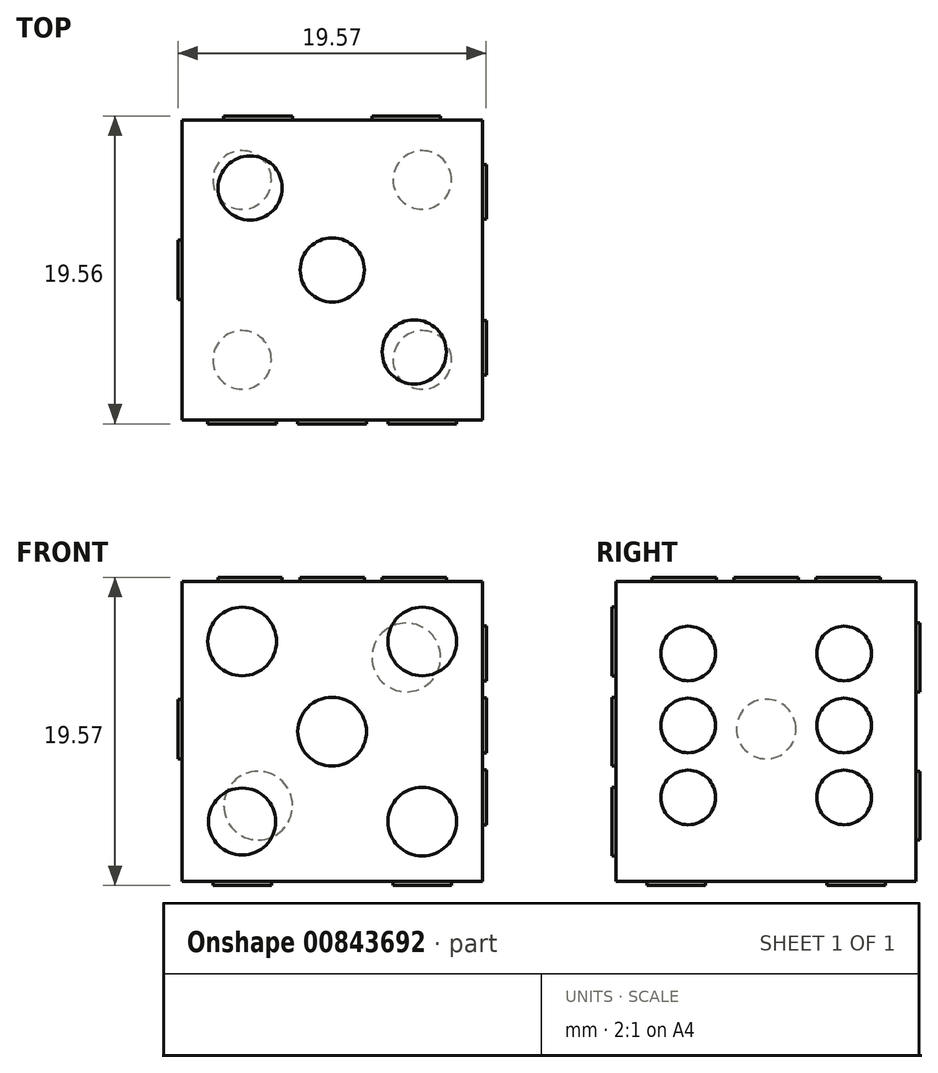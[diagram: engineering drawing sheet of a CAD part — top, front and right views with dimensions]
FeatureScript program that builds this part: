
annotation { "Feature Type Name" : "Feature", "Feature Type Description" : "" }
export const myFeature = defineFeature(function(context is Context, id is Id, definition is map)
    precondition{}
    {
        {
            var Q0;
            Q0=qCreatedBy(makeId("Front.planeOp"),FACE);
            var sketch = newSketch(context, id + "F0", { "sketchPlane" : qUnion([Q0])});
            skLineSegment(sketch, "E0", {"start": v(1.99, 4.8) * mm, "end": v(1.99, 23.85) * mm});
            skLineSegment(sketch, "E1", {"start": v(1.99, 23.85) * mm, "end": v(21.05, 23.85) * mm});
            skLineSegment(sketch, "E2", {"start": v(21.05, 23.85) * mm, "end": v(21.05, 4.8) * mm});
            skLineSegment(sketch, "E3", {"start": v(21.05, 4.8) * mm, "end": v(1.99, 4.8) * mm});
            skSolve(sketch);
        }
        {
            var Q0;
            Q0 = qSketchRegion(id + "F0", true);
            extrude(context, id + "F1", {"entities" : qUnion([Q0]), "endBound" : BoundingType.SYMMETRIC, "depth" : 19.05 * mm, "offsetDistance" : 25.4 * mm});
        }
        {
            var Q0;
            Q0=makeQuery(id+"F1.opExtrude","SWEPT_FACE",FACE,{"disambiguationData":[OSD([sQuery(id+"F0.wireOp",EDGE,"E0")])]});
            var sketch = newSketch(context, id + "F2", { "sketchPlane" : qUnion([Q0])});
            skCircle(sketch, "E4", {"center": v(0, 14.48) * mm, "radius": 1.89 * mm});
            skSolve(sketch);
        }
        {
            var Q0;
            Q0=makeQuery(id+"F1.opExtrude","SWEPT_FACE",FACE,{"disambiguationData":[OSD([sQuery(id+"F0.wireOp",EDGE,"E2")])]});
            var sketch = newSketch(context, id + "F3", { "sketchPlane" : qUnion([Q0])});
            skPoint(sketch, "E5.centerSnap0", {"position": v(-9.53, 14.32) * mm});
            skCircle(sketch, "E6", {"center": v(-4.95, 19.28) * mm, "radius": 1.73 * mm});
            skCircle(sketch, "E7", {"center": v(4.95, 19.28) * mm, "radius": 1.73 * mm});
            skCircle(sketch, "E8", {"center": v(4.95, 10.14) * mm, "radius": 1.73 * mm});
            skCircle(sketch, "E9", {"center": v(-4.95, 10.14) * mm, "radius": 1.73 * mm});
            skCircle(sketch, "E10", {"center": v(-4.95, 14.7) * mm, "radius": 1.73 * mm});
            skCircle(sketch, "E11", {"center": v(4.95, 14.7) * mm, "radius": 1.73 * mm});
            skSolve(sketch);
        }
        {
            var Q0;
            Q0=makeQuery(id+"F1.opExtrude","CAP_FACE",FACE,{"disambiguationData":[OSD([sQuery(id+"F0.wireOp",EDGE,"E0"),sQuery(id+"F0.wireOp",EDGE,"E1"),sQuery(id+"F0.wireOp",EDGE,"E2"),sQuery(id+"F0.wireOp",EDGE,"E3")])],"isStart":true});
            var sketch = newSketch(context, id + "F4", { "sketchPlane" : qUnion([Q0])});
            skCircle(sketch, "E12", {"center": v(-16.22, 19.03) * mm, "radius": 2.18 * mm});
            skCircle(sketch, "E13", {"center": v(-6.81, 9.62) * mm, "radius": 2.18 * mm});
            skSolve(sketch);
        }
        {
            var Q0;
            Q0=makeQuery(id+"F1.opExtrude","SWEPT_FACE",FACE,{"disambiguationData":[OSD([sQuery(id+"F0.wireOp",EDGE,"E1")])]});
            var sketch = newSketch(context, id + "F5", { "sketchPlane" : qUnion([Q0])});
            skCircle(sketch, "E14", {"center": v(16.73, -5.2) * mm, "radius": 2.04 * mm});
            skCircle(sketch, "E15", {"center": v(11.52, 0) * mm, "radius": 2.04 * mm});
            skCircle(sketch, "E16", {"center": v(6.3, 5.2) * mm, "radius": 2.04 * mm});
            skSolve(sketch);
        }
        {
            var Q0;
            Q0=makeQuery(id+"F1.opExtrude","SWEPT_FACE",FACE,{"disambiguationData":[OSD([sQuery(id+"F0.wireOp",EDGE,"E3")])]});
            var sketch = newSketch(context, id + "F6", { "sketchPlane" : qUnion([Q0])});
            skCircle(sketch, "E17", {"center": v(5.8, 5.72) * mm, "radius": 1.86 * mm});
            skCircle(sketch, "E18", {"center": v(17.24, 5.72) * mm, "radius": 1.86 * mm});
            skCircle(sketch, "E19", {"center": v(5.8, -5.71) * mm, "radius": 1.86 * mm});
            skCircle(sketch, "E20", {"center": v(17.24, -5.72) * mm, "radius": 1.86 * mm});
            skSolve(sketch);
        }
        {
            var Q0;
            Q0=makeQuery(id+"F1.opExtrude","CAP_FACE",FACE,{"disambiguationData":[OSD([sQuery(id+"F0.wireOp",EDGE,"E0"),sQuery(id+"F0.wireOp",EDGE,"E1"),sQuery(id+"F0.wireOp",EDGE,"E2"),sQuery(id+"F0.wireOp",EDGE,"E3")])],"isStart":false});
            var sketch = newSketch(context, id + "F7", { "sketchPlane" : qUnion([Q0])});
            skCircle(sketch, "E21", {"center": v(5.8, 8.6) * mm, "radius": 2.13 * mm});
            skCircle(sketch, "E22", {"center": v(17.24, 20.04) * mm, "radius": 2.18 * mm});
            skCircle(sketch, "E23", {"center": v(5.8, 20.04) * mm, "radius": 2.18 * mm});
            skCircle(sketch, "E24", {"center": v(17.24, 8.6) * mm, "radius": 2.18 * mm});
            skCircle(sketch, "E25", {"center": v(11.51, 14.32) * mm, "radius": 2.18 * mm});
            skSolve(sketch);
        }
        {
            var Q0;
            Q0 = qSketchRegion(id + "F2", true);
            extrude(context, id + "F8", {"entities" : qUnion([Q0]), "operationType" : NewBodyOperationType.ADD, "depth" : 0.25 * mm, "offsetDistance" : 25.4 * mm});
        }
        {
            var Q0;
            Q0 = qSketchRegion(id + "F3", true);
            extrude(context, id + "F9", {"entities" : qUnion([Q0]), "operationType" : NewBodyOperationType.ADD, "depth" : 0.25 * mm, "offsetDistance" : 25.4 * mm});
        }
        {
            var Q0;
            Q0 = qSketchRegion(id + "F4", true);
            extrude(context, id + "F10", {"entities" : qUnion([Q0]), "operationType" : NewBodyOperationType.ADD, "depth" : 0.25 * mm, "offsetDistance" : 25.4 * mm});
        }
        {
            var Q0;
            Q0 = qSketchRegion(id + "F5", true);
            extrude(context, id + "F11", {"entities" : qUnion([Q0]), "operationType" : NewBodyOperationType.ADD, "depth" : 0.25 * mm, "offsetDistance" : 25.4 * mm});
        }
        {
            var Q0;
            Q0 = qSketchRegion(id + "F6", true);
            extrude(context, id + "F12", {"entities" : qUnion([Q0]), "operationType" : NewBodyOperationType.ADD, "depth" : 0.25 * mm, "offsetDistance" : 25.4 * mm});
        }
        {
            var Q0;
            Q0 = qSketchRegion(id + "F7", true);
            extrude(context, id + "F13", {"entities" : qUnion([Q0]), "operationType" : NewBodyOperationType.ADD, "depth" : 0.25 * mm, "offsetDistance" : 25.4 * mm});
        }
    });
